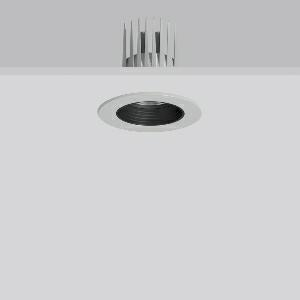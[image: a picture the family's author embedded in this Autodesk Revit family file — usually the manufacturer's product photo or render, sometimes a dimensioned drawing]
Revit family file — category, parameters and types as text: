
# Revit family: heledon_mini_e_901744_004_2_a95b
name_source: partatom
category: Lighting Fixtures
units: mm (PartAtom-declared; Revit-internal decimal feet)

## family parameters
Cut with Voids When Loaded = No
Host = Face
Light Source = No
Part Type = Normal
Room Calculation Point = No
Round Connector Dimension = Use Diameter
Shared = No

## types (1)
- HELEDON mini E (1 x LED Modul 927, 2000 lm, 2700)
    Apparent Load = 20 VA
    Approval mark = CE
    CIE Flux Codes = 96 100 100 100 100
    Color Rendering = 92
    Color Temperature = 2700
    Default Elevation = 1800 mm
    Description = Series: HELEDON mini
Round recessed downlight. Housing: die-cast aluminium, powder-coated. Black plastic ring and recessed LED to prevent glare from the side. Optical assembly with lens made of plastic (polycarbonate) for the best homogeneous light distribution - can be changed without tools. Best colour rendering index Ra>90. Suitable for Recessed ceiling mounting. Installation without tools thanks to spring fastening system. Including separate LED converter with connecting cable 600 mm.High quality converter without flickering and stroboscopic effect. Through-wiring box (5 pole) available as accessory. The following accessories can be mounted without use of tools: interchangeable lenses, decorative glasses, honeycomb louvre, clear and frosted diffusers, white interchangeable plastic ring. 
Colour: silver
Diameter: 124 mm
Height: 3 mm
Cut-out diameter: 114 mm
Recess height: 170 mm
Luminaire: recess height: 120 mm
Lamp: LED
Socket: without socket
Colour temperature: 2700K
Colour rendering index (CRI): 92
System power: 20 W
Rated luminous flux: 2000 lm
Luminous efficiency: 100 lm/W
Control gear: Regulated power supply
Protection class: II
Type of protection: IP 20
    Height = 0 mm  [stored 0 ft]
    Lamp = 1 x LED Modul 927
    Lamp Light Flux = 2000 lm
    Lamp count = 1
    Length = 124 mm  [stored 0.406824 ft]
    Lifetime = 50000 h
    Luminous efficacy = 100 lm/W
    Manufacturer = RZB
    ModVariant = No
    Model = 901744.004.2
    Mounting Place = Ceiling
    Mounting Type = Recessed
    Number of Poles = 1
    OnlyDefault = Yes
    Power Factor = 1
    Product Name = HELEDON mini E
    Product group = Recessed downlights
    ProductGroupID = 402
    Protection Class = Protection class II
    Protection Degree = IP 20
    RLX_Detail_Level = 1
    RLX_Emergency_Light_Flux = 0 lm
    RLX_Emergency_Type = 0
    RLX_Emergency_Type_DB = No
    RlxData = <blob elided: 127169 chars, md5=ee2041dc>
    Socket = socket
    Standby Power = 0 W
    System Light Flux = 2000 lm
    System Power = 20 W
    Type Comments = Product without accessories
    Type Image = 901656.004.jpg
    URL = http://relux.com
    VarID = ---
    Voltage = 230 V
    Voltage Range = 220-240 V
    Weight = 0.00 kg
    Width = 0 mm  [stored 0 ft]

note: [stored X ft] marks values corroborated as IEEE doubles in the binary element streams (Revit-internal decimal feet)

## geometry (parser evidence)
native form markers: Blend x4, Sweep x10
no freeform markers — native parametric forms only
